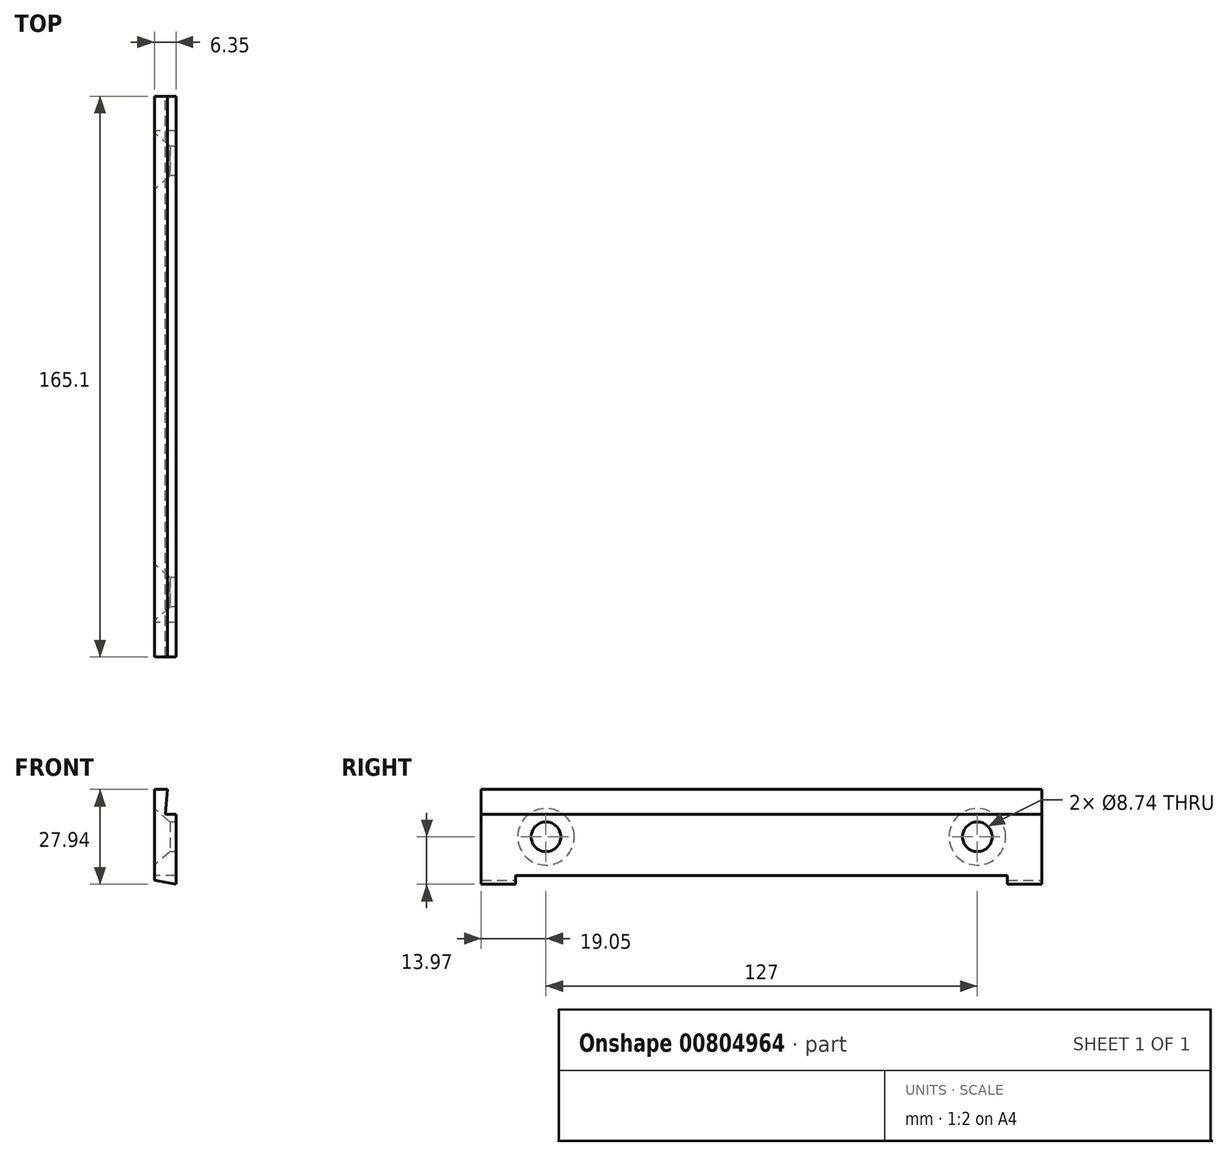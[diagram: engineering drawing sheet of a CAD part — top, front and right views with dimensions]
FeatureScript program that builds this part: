
annotation { "Feature Type Name" : "Feature", "Feature Type Description" : "" }
export const myFeature = defineFeature(function(context is Context, id is Id, definition is map)
    precondition{}
    {
        {
            var Q0;
            Q0=qCreatedBy(makeId("Front.planeOp"),FACE);
            var sketch = newSketch(context, id + "F0", { "sketchPlane" : qUnion([Q0])});
            skLineSegment(sketch, "E0.bottom", {"start": v(0, 0) * mm, "end": v(6.35, 0) * mm});
            skLineSegment(sketch, "E0.top", {"start": v(0, 25.4) * mm, "end": v(3.8, 25.4) * mm});
            skLineSegment(sketch, "E0.left", {"start": v(0, 0) * mm, "end": v(0, 25.4) * mm});
            skLineSegment(sketch, "E0.right", {"start": v(6.35, 0) * mm, "end": v(6.35, 18.03) * mm});
            skLineSegment(sketch, "E1", {"start": v(3.8, 25.4) * mm, "end": v(3.21, 18.03) * mm});
            skLineSegment(sketch, "E2", {"start": v(3.21, 18.03) * mm, "end": v(6.35, 18.03) * mm});
            skSolve(sketch);
        }
        {
            var Q0;
            Q0 = qSketchRegion(id + "F0", true);
            extrude(context, id + "F1", {"entities" : qUnion([Q0]), "depth" : 165.1 * mm, "offsetDistance" : 25.4 * mm});
        }
        {
            var Q0;
            Q0=makeQuery(id+"F1.opExtrude","SWEPT_FACE",FACE,{"disambiguationData":[OSD([sQuery(id+"F0.wireOp",EDGE,"E0.left")])]});
            var sketch = newSketch(context, id + "F2", { "sketchPlane" : qUnion([Q0])});
            skPoint(sketch, "E3", {"position": v(19.05, 11.43) * mm});
            skPoint(sketch, "E4", {"position": v(82.55, 11.43) * mm});
            skPoint(sketch, "E5", {"position": v(146.05, 11.43) * mm});
            skSolve(sketch);
        }
        {
            var Q0;
            Q0=sQuery(id+"F2.wireOp",VERTEX,"E3");
            var Q1;
            Q1=sQuery(id+"F2.wireOp",VERTEX,"E5");
            var Q2;
            Q2=makeQuery(id+"F1.opExtrude","SWEPT_BODY",BODY,{"disambiguationData":[OSD([sQuery(id+"F0.wireOp",EDGE,"E0.bottom"),sQuery(id+"F0.wireOp",EDGE,"E0.top"),sQuery(id+"F0.wireOp",EDGE,"E0.left"),sQuery(id+"F0.wireOp",EDGE,"E0.right"),sQuery(id+"F0.wireOp",EDGE,"E1"),sQuery(id+"F0.wireOp",EDGE,"E2")])]});
            hole(context, id + "F3", {"style" : HoleStyle.C_SINK, "endStyle" : HoleEndStyle.THROUGH, "standardTappedOrClearance" : lookupTablePath({ "fit" : "Normal (ASME)", "standard" : "ANSI", "size" : "5/16", "type" : "Clearance" }), "standardBlindInLast" : lookupTablePath({ "fit" : "Normal", "standard" : "ANSI", "engagement" : "75%", "pitch" : "18 tpi", "size" : "5/16", "type" : "Clearance & tapped" }), "holeDiameter" : 8.74 * mm, "cSinkDiameter" : 16.66 * mm, "cSinkAngle" : 82 * degree, "majorDiameter" : 7.94 * mm, "isTappedThrough" : true, "tappedDepth" : 12.24 * mm, "tapClearance" : 3, "startFromSketch" : true, "locations" : qUnion([Q0, Q1]), "scope" : qUnion([Q2])});
        }
        {
            var Q0;
            Q0=makeQuery(id+"F1.opExtrude","SWEPT_FACE",FACE,{"disambiguationData":[OSD([sQuery(id+"F0.wireOp",EDGE,"E0.bottom")])]});
            var sketch = newSketch(context, id + "F4", { "sketchPlane" : qUnion([Q0])});
            skLineSegment(sketch, "E6.bottom", {"start": v(6.35, 165.1) * mm, "end": v(0, 165.1) * mm});
            skLineSegment(sketch, "E6.top", {"start": v(6.35, 154.94) * mm, "end": v(0, 154.94) * mm});
            skLineSegment(sketch, "E6.left", {"start": v(6.35, 165.1) * mm, "end": v(6.35, 154.94) * mm});
            skLineSegment(sketch, "E6.right", {"start": v(0, 165.1) * mm, "end": v(0, 154.94) * mm});
            skLineSegment(sketch, "E7", {"start": v(6.35, 82.55) * mm, "end": v(0, 82.55) * mm, "construction": true});
            skLineSegment(sketch, "E8.MirrorCS", {"start": v(6.35, 10.16) * mm, "end": v(0, 10.16) * mm});
            skLineSegment(sketch, "E9.MirrorCS", {"start": v(0, 0) * mm, "end": v(0, 10.16) * mm});
            skLineSegment(sketch, "E10.MirrorCS", {"start": v(6.35, 0) * mm, "end": v(6.35, 10.16) * mm});
            skLineSegment(sketch, "E11.MirrorCS", {"start": v(6.35, 0) * mm, "end": v(0, 0) * mm});
            skSolve(sketch);
        }
        {
            var Q0;
            Q0 = qSketchRegion(id + "F4", true);
            extrude(context, id + "F5", {"entities" : qUnion([Q0]), "operationType" : NewBodyOperationType.ADD, "depth" : 2.54 * mm, "offsetDistance" : 25.4 * mm});
        }
        {
            var Q0;
            Q0=makeQuery(id+"F5.boolean.opBoolean","MERGE",FACE,{"derivedFrom":[makeQuery(id+"F1.opExtrude","CAP_FACE",FACE,{"disambiguationData":[OSD([sQuery(id+"F0.wireOp",EDGE,"E0.bottom"),sQuery(id+"F0.wireOp",EDGE,"E0.top"),sQuery(id+"F0.wireOp",EDGE,"E0.left"),sQuery(id+"F0.wireOp",EDGE,"E0.right"),sQuery(id+"F0.wireOp",EDGE,"E1"),sQuery(id+"F0.wireOp",EDGE,"E2")])],"isStart":true}),makeQuery(id+"F5.opExtrude","SWEPT_FACE",FACE,{"disambiguationData":[OSD([sQuery(id+"F4.wireOp",EDGE,"E11.MirrorCS")])]})]});
            var sketch = newSketch(context, id + "F6", { "sketchPlane" : qUnion([Q0])});
            skLineSegment(sketch, "E12", {"start": v(-6.35, -2.54) * mm, "end": v(0, -1.42) * mm});
            skLineSegment(sketch, "E13", {"start": v(0, -1.42) * mm, "end": v(-6.35, -1.42) * mm});
            skLineSegment(sketch, "E14", {"start": v(-6.35, -1.42) * mm, "end": v(-6.35, -2.54) * mm});
            skSolve(sketch);
        }
        {
            var Q0;
            {var subQ0=sQuery(id+"F6.wireOp",EDGE,"E12");Q0=makeQuery(id+"F6.imprint","IMPRINT",FACE,{"disambiguationData":[TD([[makeQuery(id+"F6.imprint","IMPRINT",EDGE,{"derivedFrom":subQ0}),-1.0]])]});}
            extrude(context, id + "F7", {"entities" : qUnion([Q0]), "operationType" : NewBodyOperationType.REMOVE, "endBound" : BoundingType.THROUGH_ALL, "oppositeDirection" : true, "depth" : 25.4 * mm, "offsetDistance" : 25.4 * mm});
        }
    });
